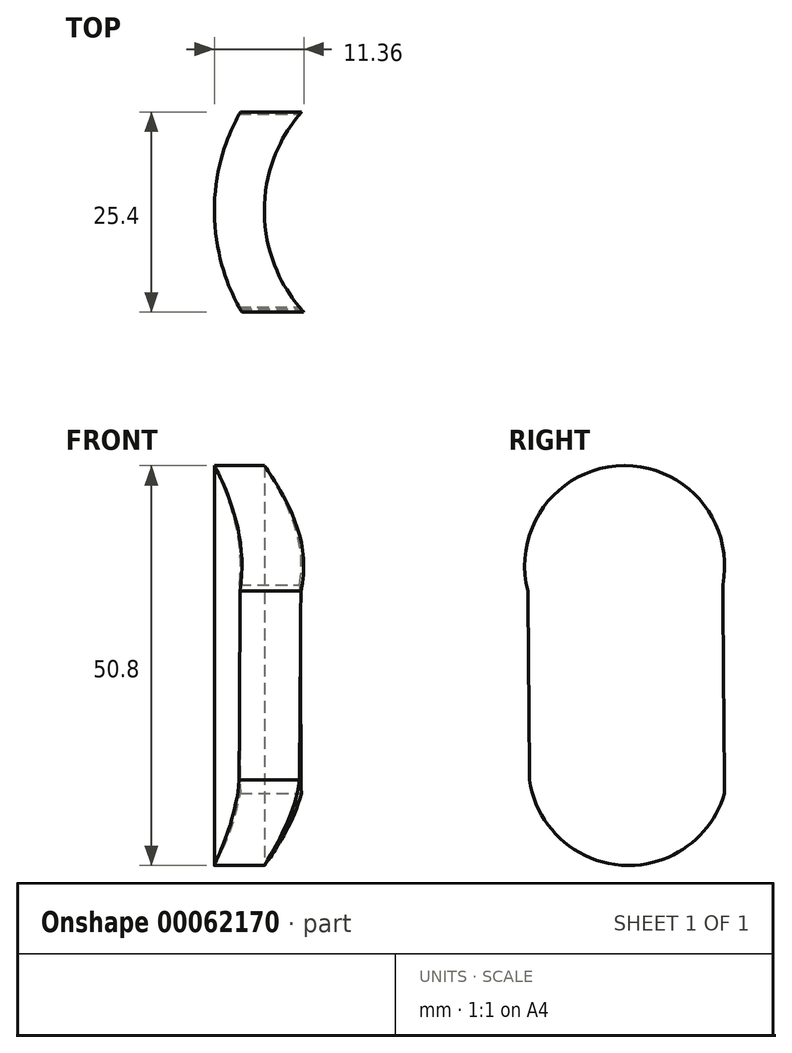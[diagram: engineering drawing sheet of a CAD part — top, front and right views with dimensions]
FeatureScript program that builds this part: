
annotation { "Feature Type Name" : "Feature", "Feature Type Description" : "" }
export const myFeature = defineFeature(function(context is Context, id is Id, definition is map)
    precondition{}
    {
        {
            var Q0;
            Q0=qCreatedBy(makeId("Top.planeOp"),FACE);
            var sketch = newSketch(context, id + "F0", { "sketchPlane" : qUnion([Q0])});
            skCircle(sketch, "E0", {"center": v(0, 0) * mm, "radius": 19.05 * mm});
            skCircle(sketch, "E1", {"center": v(0, 0) * mm, "radius": 25.4 * mm});
            skSolve(sketch);
        }
        {
            var Q0;
            Q0 = qSketchRegion(id + "F0", true);
            extrude(context, id + "F1", {"entities" : qUnion([Q0]), "endBound" : BoundingType.SYMMETRIC, "depth" : 50.8 * mm});
        }
        {
            var Q0;
            Q0=qCreatedBy(makeId("Right.planeOp"),FACE);
            var sketch = newSketch(context, id + "F2", { "sketchPlane" : qUnion([Q0])});
            skLineSegment(sketch, "E2.rect.left", {"start": v(12.3, 10.26) * mm, "end": v(12.52, -16.22) * mm});
            skLineSegment(sketch, "E2.rect.right", {"start": v(-12.46, 9.5) * mm, "end": v(-12.25, -14.5) * mm});
            skPoint(sketch, "E2.rect.middle", {"position": v(0, 0) * mm});
            skArc(sketch, "E3", {"start": v(12.3, 10.26) * mm, "mid": v(-0.57, 25.4) * mm, "end": v(-12.46, 9.5) * mm});
            skPoint(sketch, "E3.first.point", {"position": v(-0.22, 25.4) * mm});
            skPoint(sketch, "E3.second.point", {"position": v(12.3, 10.26) * mm});
            skPoint(sketch, "E3.third.point", {"position": v(-12.46, 9.5) * mm});
            skArc(sketch, "E4", {"start": v(-12.25, -14.5) * mm, "mid": v(-0.56, -25.37) * mm, "end": v(12.52, -16.22) * mm});
            skPoint(sketch, "E4.first.point", {"position": v(0.22, -25.4) * mm});
            skPoint(sketch, "E4.second.point", {"position": v(12.52, -16.22) * mm});
            skPoint(sketch, "E4.third.point", {"position": v(-12.25, -14.5) * mm});
            skPoint(sketch, "E5.orphan", {"position": v(-12.6, 25.36) * mm});
            skPoint(sketch, "E6.orphan", {"position": v(12.16, 25.44) * mm});
            skPoint(sketch, "E7.orphan", {"position": v(-12.16, -25.44) * mm});
            skPoint(sketch, "E8.orphan", {"position": v(12.6, -25.36) * mm});
            skLineSegment(sketch, "E9.rect.bottom", {"start": v(-39.05, -50.17) * mm, "end": v(108.8, -50.17) * mm});
            skLineSegment(sketch, "E9.rect.top", {"start": v(-39.05, 123.38) * mm, "end": v(108.8, 123.38) * mm});
            skLineSegment(sketch, "E9.rect.left", {"start": v(-39.05, -50.17) * mm, "end": v(-39.05, 123.38) * mm});
            skLineSegment(sketch, "E9.rect.right", {"start": v(108.8, -50.17) * mm, "end": v(108.8, 123.38) * mm});
            skPoint(sketch, "E9.rect.middle", {"position": v(34.87, 36.6) * mm});
            skSolve(sketch);
        }
        {
            var Q0;
            Q0 = qSketchRegion(id + "F2", true);
            extrude(context, id + "F3", {"entities" : qUnion([Q0]), "operationType" : NewBodyOperationType.REMOVE, "oppositeDirection" : true, "depth" : 25.4 * mm});
        }
        {
            var Q0;
            Q0=qCreatedBy(makeId("Front.planeOp"),FACE);
            var sketch = newSketch(context, id + "F4", { "sketchPlane" : qUnion([Q0])});
            skLineSegment(sketch, "E10.bottom", {"start": v(-2.95, 39.24) * mm, "end": v(34.67, 39.24) * mm});
            skLineSegment(sketch, "E10.top", {"start": v(-2.95, -39.92) * mm, "end": v(34.67, -39.92) * mm});
            skLineSegment(sketch, "E10.left", {"start": v(-2.95, 39.24) * mm, "end": v(-2.95, -39.92) * mm});
            skLineSegment(sketch, "E10.right", {"start": v(34.67, 39.24) * mm, "end": v(34.67, -39.92) * mm});
            skSolve(sketch);
        }
        {
            var Q0;
            Q0 = qSketchRegion(id + "F4", true);
            extrude(context, id + "F5", {"entities" : qUnion([Q0]), "operationType" : NewBodyOperationType.REMOVE, "endBound" : BoundingType.SYMMETRIC, "oppositeDirection" : true, "depth" : 533.4 * mm});
        }
        {
            var Q0;
            Q0=qCreatedBy(makeId("Front.planeOp"),FACE);
            var sketch = newSketch(context, id + "F6", { "sketchPlane" : qUnion([Q0])});
            skLineSegment(sketch, "E11.bottom", {"start": v(-5.36, 32.49) * mm, "end": v(37.25, 32.49) * mm});
            skLineSegment(sketch, "E11.top", {"start": v(-5.36, -40.6) * mm, "end": v(37.25, -40.6) * mm});
            skLineSegment(sketch, "E11.left", {"start": v(-5.36, 32.49) * mm, "end": v(-5.36, -40.6) * mm});
            skLineSegment(sketch, "E11.right", {"start": v(37.25, 32.49) * mm, "end": v(37.25, -40.6) * mm});
            skSolve(sketch);
        }
        {
            var Q0;
            Q0 = qSketchRegion(id + "F6", true);
            extrude(context, id + "F7", {"entities" : qUnion([Q0]), "operationType" : NewBodyOperationType.REMOVE, "endBound" : BoundingType.SYMMETRIC, "oppositeDirection" : true, "depth" : 50.8 * mm});
        }
    });
